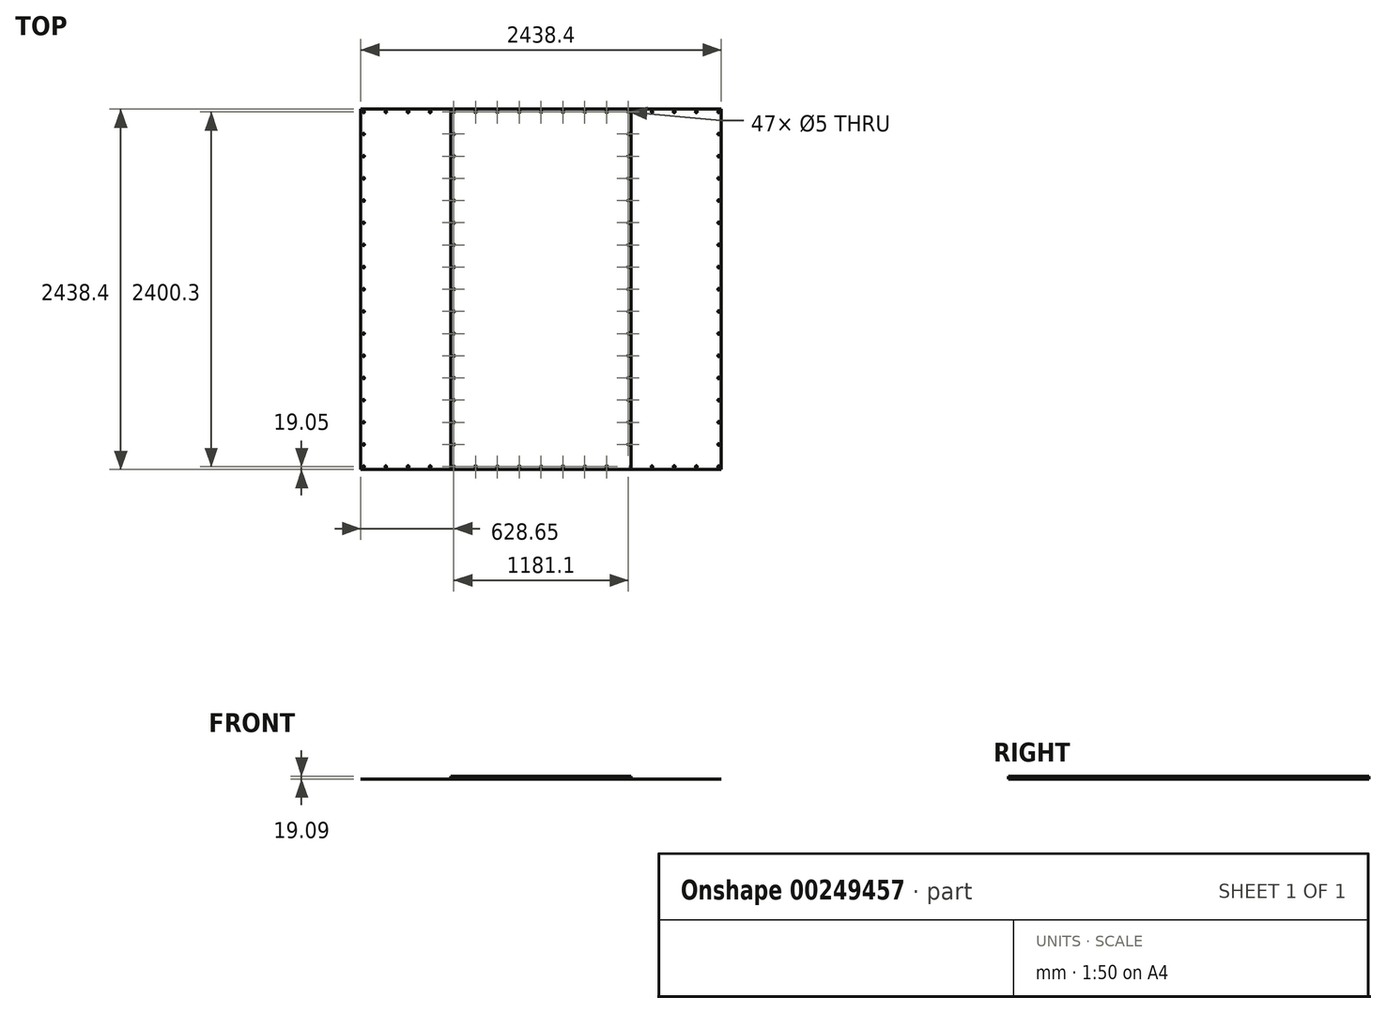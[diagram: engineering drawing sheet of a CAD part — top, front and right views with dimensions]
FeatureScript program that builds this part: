
annotation { "Feature Type Name" : "Feature", "Feature Type Description" : "" }
export const myFeature = defineFeature(function(context is Context, id is Id, definition is map)
    precondition{}
    {
        {
            var Q0;
            Q0=qCreatedBy(makeId("Top.planeOp"),FACE);
            var sketch = newSketch(context, id + "F0", { "sketchPlane" : qUnion([Q0])});
            skLineSegment(sketch, "E0.bottom", {"start": v(0, 1219.2) * mm, "end": v(1219.2, 1219.2) * mm});
            skLineSegment(sketch, "E0.top", {"start": v(0, -1219.2) * mm, "end": v(1219.2, -1219.2) * mm});
            skLineSegment(sketch, "E0.left", {"start": v(0, 1219.2) * mm, "end": v(0, -1219.2) * mm});
            skLineSegment(sketch, "E0.right", {"start": v(1219.2, 1219.2) * mm, "end": v(1219.2, -1219.2) * mm});
            skLineSegment(sketch, "E1", {"start": v(1219.2, 0) * mm, "end": v(0, 0) * mm});
            skSolve(sketch);
        }
        {
            var Q0;
            Q0 = qSketchRegion(id + "F0", true);
            extrude(context, id + "F1", {"entities" : qUnion([Q0]), "depth" : 5 / 203.2 * mm});
        }
        {
            var Q0;
            Q0=qCreatedBy(makeId("Top.planeOp"),FACE);
            var sketch = newSketch(context, id + "F2", { "sketchPlane" : qUnion([Q0])});
            skLineSegment(sketch, "E2.bottom", {"start": v(-1219.2, 1219.2) * mm, "end": v(0, 1219.2) * mm});
            skLineSegment(sketch, "E2.top", {"start": v(-1219.2, -1219.2) * mm, "end": v(0, -1219.2) * mm});
            skLineSegment(sketch, "E2.left", {"start": v(-1219.2, 1219.2) * mm, "end": v(-1219.2, -1219.2) * mm});
            skLineSegment(sketch, "E2.right", {"start": v(0, 1219.2) * mm, "end": v(0, -1219.2) * mm});
            skSolve(sketch);
        }
        {
            var Q0;
            Q0 = qSketchRegion(id + "F2", true);
            extrude(context, id + "F3", {"entities" : qUnion([Q0]), "operationType" : NewBodyOperationType.ADD, "depth" : 5 / 203.2 * mm});
        }
        {
            var Q0;
            Q0=makeQuery(id+"F3.boolean.opBoolean","MERGE",FACE,{"derivedFrom":[makeQuery(id+"F1.opExtrude","CAP_FACE",FACE,{"disambiguationData":[OSD([sQuery(id+"F0.wireOp",EDGE,"E0.bottom"),sQuery(id+"F0.wireOp",EDGE,"E0.top"),sQuery(id+"F0.wireOp",EDGE,"E0.left"),sQuery(id+"F0.wireOp",EDGE,"E0.right")])],"isStart":true}),makeQuery(id+"F3.opExtrude","CAP_FACE",FACE,{"disambiguationData":[OSD([sQuery(id+"F2.wireOp",EDGE,"E2.bottom"),sQuery(id+"F2.wireOp",EDGE,"E2.top"),sQuery(id+"F2.wireOp",EDGE,"E2.left"),sQuery(id+"F2.wireOp",EDGE,"E2.right")])],"isStart":true})]});
            var sketch = newSketch(context, id + "F4", { "sketchPlane" : qUnion([Q0])});
            skLineSegment(sketch, "E3.bottom", {"start": v(1219.2, -1219.2) * mm, "end": v(-1219.2, -1219.2) * mm});
            skLineSegment(sketch, "E3.top", {"start": v(1219.2, 0) * mm, "end": v(-1219.2, 0) * mm});
            skLineSegment(sketch, "E3.left", {"start": v(1219.2, -1219.2) * mm, "end": v(1219.2, 0) * mm});
            skLineSegment(sketch, "E3.right", {"start": v(-1219.2, -1219.2) * mm, "end": v(-1219.2, 0) * mm});
            skSolve(sketch);
        }
        {
            var Q0;
            Q0 = qSketchRegion(id + "F4", true);
            extrude(context, id + "F5", {"entities" : qUnion([Q0]), "operationType" : NewBodyOperationType.ADD, "depth" : 5 / 203.2 * mm});
        }
        {
            var Q0;
            Q0=makeQuery(id+"F3.boolean.opBoolean","MERGE",FACE,{"derivedFrom":[makeQuery(id+"F1.opExtrude","CAP_FACE",FACE,{"disambiguationData":[OSD([sQuery(id+"F0.wireOp",EDGE,"E0.bottom"),sQuery(id+"F0.wireOp",EDGE,"E0.top"),sQuery(id+"F0.wireOp",EDGE,"E0.left"),sQuery(id+"F0.wireOp",EDGE,"E0.right")])],"isStart":true}),makeQuery(id+"F3.opExtrude","CAP_FACE",FACE,{"disambiguationData":[OSD([sQuery(id+"F2.wireOp",EDGE,"E2.bottom"),sQuery(id+"F2.wireOp",EDGE,"E2.top"),sQuery(id+"F2.wireOp",EDGE,"E2.left"),sQuery(id+"F2.wireOp",EDGE,"E2.right")])],"isStart":true})]});
            var sketch = newSketch(context, id + "F6", { "sketchPlane" : qUnion([Q0])});
            skLineSegment(sketch, "E4.bottom", {"start": v(-1219.2, 1219.2) * mm, "end": v(1219.2, 1219.2) * mm});
            skLineSegment(sketch, "E4.top", {"start": v(-1219.2, 0) * mm, "end": v(1219.2, 0) * mm});
            skLineSegment(sketch, "E4.left", {"start": v(-1219.2, 1219.2) * mm, "end": v(-1219.2, 0) * mm});
            skLineSegment(sketch, "E4.right", {"start": v(1219.2, 1219.2) * mm, "end": v(1219.2, 0) * mm});
            skSolve(sketch);
        }
        {
            var Q0;
            Q0 = qSketchRegion(id + "F6", true);
            extrude(context, id + "F7", {"entities" : qUnion([Q0]), "operationType" : NewBodyOperationType.ADD, "depth" : 5 / 203.2 * mm});
        }
        {
            var Q0;
            Q0=makeQuery(id+"F3.boolean.opBoolean","MERGE",FACE,{"derivedFrom":[makeQuery(id+"F1.opExtrude","CAP_FACE",FACE,{"disambiguationData":[OSD([sQuery(id+"F0.wireOp",EDGE,"E0.bottom"),sQuery(id+"F0.wireOp",EDGE,"E0.top"),sQuery(id+"F0.wireOp",EDGE,"E0.left"),sQuery(id+"F0.wireOp",EDGE,"E0.right")])],"isStart":false}),makeQuery(id+"F3.opExtrude","CAP_FACE",FACE,{"disambiguationData":[OSD([sQuery(id+"F2.wireOp",EDGE,"E2.bottom"),sQuery(id+"F2.wireOp",EDGE,"E2.top"),sQuery(id+"F2.wireOp",EDGE,"E2.left"),sQuery(id+"F2.wireOp",EDGE,"E2.right")])],"isStart":false})]});
            var sketch = newSketch(context, id + "F8", { "sketchPlane" : qUnion([Q0])});
            skLineSegment(sketch, "E5", {"start": v(-1219.2, -1219.2) * mm, "end": v(-1200.15, -1200.15) * mm});
            skLineSegment(sketch, "E6", {"start": v(-1200.15, -1200.15) * mm, "end": v(-1050.13, -1200.15) * mm});
            skLineSegment(sketch, "E7", {"start": v(-1050.13, -1200.15) * mm, "end": v(-900.11, -1200.15) * mm});
            skLineSegment(sketch, "E8", {"start": v(-900.11, -1200.15) * mm, "end": v(-750.1, -1200.15) * mm});
            skLineSegment(sketch, "E9", {"start": v(-750.1, -1200.15) * mm, "end": v(-600.08, -1200.15) * mm});
            skLineSegment(sketch, "E10", {"start": v(-600.08, -1200.15) * mm, "end": v(-450.06, -1200.15) * mm});
            skLineSegment(sketch, "E11", {"start": v(-450.06, -1200.15) * mm, "end": v(-300.04, -1200.15) * mm});
            skLineSegment(sketch, "E12", {"start": v(-300.04, -1200.15) * mm, "end": v(-150.02, -1200.15) * mm});
            skLineSegment(sketch, "E13", {"start": v(-150.02, -1200.15) * mm, "end": v(0, -1200.15) * mm});
            skLineSegment(sketch, "E14", {"start": v(0, -1200.15) * mm, "end": v(150.02, -1200.15) * mm});
            skLineSegment(sketch, "E15", {"start": v(150.02, -1200.15) * mm, "end": v(300.04, -1200.15) * mm});
            skLineSegment(sketch, "E16", {"start": v(300.04, -1200.15) * mm, "end": v(450.06, -1200.15) * mm});
            skLineSegment(sketch, "E17", {"start": v(450.06, -1200.15) * mm, "end": v(600.07, -1200.15) * mm});
            skLineSegment(sketch, "E18", {"start": v(600.07, -1200.15) * mm, "end": v(750.1, -1200.15) * mm});
            skLineSegment(sketch, "E19", {"start": v(750.1, -1200.15) * mm, "end": v(900.11, -1200.15) * mm});
            skLineSegment(sketch, "E20", {"start": v(900.11, -1200.15) * mm, "end": v(1050.13, -1200.15) * mm});
            skLineSegment(sketch, "E21", {"start": v(1050.13, -1200.15) * mm, "end": v(1200.15, -1200.15) * mm});
            skLineSegment(sketch, "E22", {"start": v(1200.15, -1200.15) * mm, "end": v(1219.2, -1219.2) * mm});
            skLineSegment(sketch, "E23", {"start": v(-1200.15, 1200.15) * mm, "end": v(-1219.2, 1219.2) * mm});
            skLineSegment(sketch, "E24", {"start": v(-1200.15, 1200.15) * mm, "end": v(-1050.13, 1200.15) * mm});
            skLineSegment(sketch, "E25", {"start": v(-1050.13, 1200.15) * mm, "end": v(-900.11, 1200.15) * mm});
            skLineSegment(sketch, "E26", {"start": v(-900.11, 1200.15) * mm, "end": v(-750.1, 1200.15) * mm});
            skLineSegment(sketch, "E27", {"start": v(-750.1, 1200.15) * mm, "end": v(-600.08, 1200.15) * mm});
            skLineSegment(sketch, "E28", {"start": v(-600.08, 1200.15) * mm, "end": v(-450.06, 1200.15) * mm});
            skLineSegment(sketch, "E29", {"start": v(-450.06, 1200.15) * mm, "end": v(-300.04, 1200.15) * mm});
            skLineSegment(sketch, "E30", {"start": v(-300.04, 1200.15) * mm, "end": v(-150.02, 1200.15) * mm});
            skLineSegment(sketch, "E31", {"start": v(-150.02, 1200.15) * mm, "end": v(0, 1200.15) * mm});
            skLineSegment(sketch, "E32", {"start": v(0, 1200.15) * mm, "end": v(150.02, 1200.15) * mm});
            skLineSegment(sketch, "E33", {"start": v(150.02, 1200.15) * mm, "end": v(300.04, 1200.15) * mm});
            skLineSegment(sketch, "E34", {"start": v(300.04, 1200.15) * mm, "end": v(450.06, 1200.15) * mm});
            skLineSegment(sketch, "E35", {"start": v(450.06, 1200.15) * mm, "end": v(600.08, 1200.15) * mm});
            skLineSegment(sketch, "E36", {"start": v(600.08, 1200.15) * mm, "end": v(750.1, 1200.15) * mm});
            skLineSegment(sketch, "E37", {"start": v(750.1, 1200.15) * mm, "end": v(900.11, 1200.15) * mm});
            skLineSegment(sketch, "E38", {"start": v(900.11, 1200.15) * mm, "end": v(1050.13, 1200.15) * mm});
            skLineSegment(sketch, "E39", {"start": v(1050.13, 1200.15) * mm, "end": v(1200.15, 1200.15) * mm});
            skLineSegment(sketch, "E40", {"start": v(1200.15, 1200.15) * mm, "end": v(1219.2, 1219.2) * mm});
            skLineSegment(sketch, "E41", {"start": v(1219.2, -1219.2) * mm, "end": v(1200.15, -1200.15) * mm});
            skLineSegment(sketch, "E42", {"start": v(1200.15, -1200.15) * mm, "end": v(1200.15, -1050.13) * mm});
            skLineSegment(sketch, "E43", {"start": v(1200.15, -1050.13) * mm, "end": v(1200.15, -900.11) * mm});
            skLineSegment(sketch, "E44", {"start": v(1200.15, -900.11) * mm, "end": v(1200.15, -750.1) * mm});
            skLineSegment(sketch, "E45", {"start": v(1200.15, -750.1) * mm, "end": v(1200.15, -600.07) * mm});
            skLineSegment(sketch, "E46", {"start": v(1200.15, -600.07) * mm, "end": v(1200.15, -450.06) * mm});
            skLineSegment(sketch, "E47", {"start": v(1200.15, -450.06) * mm, "end": v(1200.15, -300.04) * mm});
            skLineSegment(sketch, "E48", {"start": v(1200.15, -300.04) * mm, "end": v(1200.15, -150.02) * mm});
            skLineSegment(sketch, "E49", {"start": v(1200.15, -150.02) * mm, "end": v(1200.15, 0) * mm});
            skLineSegment(sketch, "E50", {"start": v(1200.15, 0) * mm, "end": v(1200.15, 150.02) * mm});
            skLineSegment(sketch, "E51", {"start": v(1200.15, 150.02) * mm, "end": v(1200.15, 300.04) * mm});
            skLineSegment(sketch, "E52", {"start": v(1200.15, 300.04) * mm, "end": v(1200.15, 450.06) * mm});
            skLineSegment(sketch, "E53", {"start": v(1200.15, 450.06) * mm, "end": v(1200.15, 600.08) * mm});
            skLineSegment(sketch, "E54", {"start": v(1200.15, 600.08) * mm, "end": v(1200.15, 750.1) * mm});
            skLineSegment(sketch, "E55", {"start": v(1200.15, 750.1) * mm, "end": v(1200.15, 900.11) * mm});
            skLineSegment(sketch, "E56", {"start": v(1200.15, 900.11) * mm, "end": v(1200.15, 1050.13) * mm});
            skLineSegment(sketch, "E57", {"start": v(1200.15, 1050.13) * mm, "end": v(1200.15, 1200.15) * mm});
            skLineSegment(sketch, "E58", {"start": v(-1219.2, 1219.2) * mm, "end": v(-1200.15, 1200.15) * mm});
            skLineSegment(sketch, "E59", {"start": v(-1200.15, 1200.15) * mm, "end": v(-1200.15, 1050.13) * mm});
            skLineSegment(sketch, "E60", {"start": v(-1200.15, 1050.13) * mm, "end": v(-1200.15, 900.11) * mm});
            skLineSegment(sketch, "E61", {"start": v(-1200.15, 900.11) * mm, "end": v(-1200.15, 750.1) * mm});
            skLineSegment(sketch, "E62", {"start": v(-1200.15, 750.1) * mm, "end": v(-1200.15, 600.07) * mm});
            skLineSegment(sketch, "E63", {"start": v(-1200.15, 600.07) * mm, "end": v(-1200.15, 450.06) * mm});
            skLineSegment(sketch, "E64", {"start": v(-1200.15, 450.06) * mm, "end": v(-1200.15, 300.04) * mm});
            skLineSegment(sketch, "E65", {"start": v(-1200.15, 300.04) * mm, "end": v(-1200.15, 150.02) * mm});
            skLineSegment(sketch, "E66", {"start": v(-1200.15, 150.02) * mm, "end": v(-1200.15, 0) * mm});
            skLineSegment(sketch, "E67", {"start": v(-1200.15, 0) * mm, "end": v(-1200.15, -150.02) * mm});
            skLineSegment(sketch, "E68", {"start": v(-1200.15, -150.02) * mm, "end": v(-1200.15, -300.04) * mm});
            skLineSegment(sketch, "E69", {"start": v(-1200.15, -300.04) * mm, "end": v(-1200.15, -450.06) * mm});
            skLineSegment(sketch, "E70", {"start": v(-1200.15, -450.06) * mm, "end": v(-1200.15, -600.08) * mm});
            skLineSegment(sketch, "E71", {"start": v(-1200.15, -600.08) * mm, "end": v(-1200.15, -750.1) * mm});
            skLineSegment(sketch, "E72", {"start": v(-1200.15, -750.1) * mm, "end": v(-1200.15, -900.11) * mm});
            skLineSegment(sketch, "E73", {"start": v(-1200.15, -900.11) * mm, "end": v(-1200.15, -1050.13) * mm});
            skLineSegment(sketch, "E74", {"start": v(-1200.15, -1050.13) * mm, "end": v(-1200.15, -1200.15) * mm});
            skLineSegment(sketch, "E75", {"start": v(-1200.15, -1200.15) * mm, "end": v(-1219.2, -1219.2) * mm});
            skSolve(sketch);
        }
        {
            var Q0;
            Q0=sQuery(id+"F8.wireOp",VERTEX,"E63.start");
            var Q1;
            Q1=sQuery(id+"F8.wireOp",VERTEX,"E64.start");
            var Q2;
            Q2=sQuery(id+"F8.wireOp",VERTEX,"E65.start");
            var Q3;
            Q3=sQuery(id+"F8.wireOp",VERTEX,"E66.start");
            var Q4;
            Q4=sQuery(id+"F8.wireOp",VERTEX,"E67.start");
            var Q5;
            Q5=sQuery(id+"F8.wireOp",VERTEX,"E68.start");
            var Q6;
            Q6=sQuery(id+"F8.wireOp",VERTEX,"E68.end");
            var Q7;
            Q7=sQuery(id+"F8.wireOp",VERTEX,"E70.start");
            var Q8;
            Q8=sQuery(id+"F8.wireOp",VERTEX,"E71.start");
            var Q9;
            Q9=sQuery(id+"F8.wireOp",VERTEX,"E72.start");
            var Q10;
            Q10=sQuery(id+"F8.wireOp",VERTEX,"E73.start");
            var Q11;
            Q11=sQuery(id+"F8.wireOp",VERTEX,"E74.start");
            var Q12;
            Q12=sQuery(id+"F8.wireOp",VERTEX,"E75.start");
            var Q13;
            Q13=sQuery(id+"F8.wireOp",VERTEX,"E7.start");
            var Q14;
            Q14=sQuery(id+"F8.wireOp",VERTEX,"E8.start");
            var Q15;
            Q15=sQuery(id+"F8.wireOp",VERTEX,"E9.start");
            var Q16;
            Q16=sQuery(id+"F8.wireOp",VERTEX,"E10.start");
            var Q17;
            Q17=sQuery(id+"F8.wireOp",VERTEX,"E11.start");
            var Q18;
            Q18=sQuery(id+"F8.wireOp",VERTEX,"E12.start");
            var Q19;
            Q19=sQuery(id+"F8.wireOp",VERTEX,"E13.start");
            var Q20;
            Q20=sQuery(id+"F8.wireOp",VERTEX,"E62.start");
            var Q21;
            Q21=sQuery(id+"F8.wireOp",VERTEX,"E60.end");
            var Q22;
            Q22=sQuery(id+"F8.wireOp",VERTEX,"E60.start");
            var Q23;
            Q23=sQuery(id+"F8.wireOp",VERTEX,"E24.start");
            var Q24;
            Q24=sQuery(id+"F8.wireOp",VERTEX,"E25.start");
            var Q25;
            Q25=sQuery(id+"F8.wireOp",VERTEX,"E26.start");
            var Q26;
            Q26=sQuery(id+"F8.wireOp",VERTEX,"E27.start");
            var Q27;
            Q27=sQuery(id+"F8.wireOp",VERTEX,"E28.start");
            var Q28;
            Q28=sQuery(id+"F8.wireOp",VERTEX,"E29.start");
            var Q29;
            Q29=sQuery(id+"F8.wireOp",VERTEX,"E29.end");
            var Q30;
            Q30=sQuery(id+"F8.wireOp",VERTEX,"E31.start");
            var Q31;
            Q31=sQuery(id+"F8.wireOp",VERTEX,"E32.start");
            var Q32;
            Q32=sQuery(id+"F8.wireOp",VERTEX,"E33.start");
            var Q33;
            Q33=sQuery(id+"F8.wireOp",VERTEX,"E34.start");
            var Q34;
            Q34=sQuery(id+"F8.wireOp",VERTEX,"E35.start");
            var Q35;
            Q35=sQuery(id+"F8.wireOp",VERTEX,"E36.start");
            var Q36;
            Q36=sQuery(id+"F8.wireOp",VERTEX,"E37.start");
            var Q37;
            Q37=sQuery(id+"F8.wireOp",VERTEX,"E37.end");
            var Q38;
            Q38=sQuery(id+"F8.wireOp",VERTEX,"E39.start");
            var Q39;
            Q39=sQuery(id+"F8.wireOp",VERTEX,"E40.start");
            var Q40;
            Q40=sQuery(id+"F8.wireOp",VERTEX,"E57.start");
            var Q41;
            Q41=sQuery(id+"F8.wireOp",VERTEX,"E56.start");
            var Q42;
            Q42=sQuery(id+"F8.wireOp",VERTEX,"E55.start");
            var Q43;
            Q43=sQuery(id+"F8.wireOp",VERTEX,"E53.end");
            var Q44;
            Q44=sQuery(id+"F8.wireOp",VERTEX,"E53.start");
            var Q45;
            Q45=sQuery(id+"F8.wireOp",VERTEX,"E52.start");
            var Q46;
            Q46=sQuery(id+"F8.wireOp",VERTEX,"E51.start");
            var Q47;
            Q47=sQuery(id+"F8.wireOp",VERTEX,"E50.start");
            var Q48;
            Q48=sQuery(id+"F8.wireOp",VERTEX,"E49.start");
            var Q49;
            Q49=sQuery(id+"F8.wireOp",VERTEX,"E48.start");
            var Q50;
            Q50=sQuery(id+"F8.wireOp",VERTEX,"E47.start");
            var Q51;
            Q51=sQuery(id+"F8.wireOp",VERTEX,"E45.end");
            var Q52;
            Q52=sQuery(id+"F8.wireOp",VERTEX,"E45.start");
            var Q53;
            Q53=sQuery(id+"F8.wireOp",VERTEX,"E44.start");
            var Q54;
            Q54=sQuery(id+"F8.wireOp",VERTEX,"E43.start");
            var Q55;
            Q55=sQuery(id+"F8.wireOp",VERTEX,"E21.end");
            var Q56;
            Q56=sQuery(id+"F8.wireOp",VERTEX,"E21.start");
            var Q57;
            Q57=sQuery(id+"F8.wireOp",VERTEX,"E20.start");
            var Q58;
            Q58=sQuery(id+"F8.wireOp",VERTEX,"E19.start");
            var Q59;
            Q59=sQuery(id+"F8.wireOp",VERTEX,"E18.start");
            var Q60;
            Q60=sQuery(id+"F8.wireOp",VERTEX,"E17.start");
            var Q61;
            Q61=sQuery(id+"F8.wireOp",VERTEX,"E16.start");
            var Q62;
            Q62=sQuery(id+"F8.wireOp",VERTEX,"E15.start");
            var Q63;
            Q63=sQuery(id+"F8.wireOp",VERTEX,"E13.end");
            var Q64;
            Q64=sQuery(id+"F8.wireOp",VERTEX,"E13.end");
            var Q65;
            Q65=sQuery(id+"F8.wireOp",VERTEX,"E15.start");
            var Q66;
            Q66=sQuery(id+"F8.wireOp",VERTEX,"E16.start");
            var Q67;
            Q67=sQuery(id+"F8.wireOp",VERTEX,"E17.start");
            var Q68;
            Q68=sQuery(id+"F8.wireOp",VERTEX,"E18.start");
            var Q69;
            Q69=sQuery(id+"F8.wireOp",VERTEX,"E19.start");
            var Q70;
            Q70=sQuery(id+"F8.wireOp",VERTEX,"E20.start");
            var Q71;
            Q71=makeQuery(id+"F1.opExtrude","SWEPT_BODY",BODY,{"disambiguationData":[OSD([sQuery(id+"F0.wireOp",EDGE,"E0.bottom"),sQuery(id+"F0.wireOp",EDGE,"E0.top"),sQuery(id+"F0.wireOp",EDGE,"E0.left"),sQuery(id+"F0.wireOp",EDGE,"E0.right")])]});
            hole(context, id + "F9", {"style" : HoleStyle.C_SINK, "endStyle" : HoleEndStyle.THROUGH, "standardTappedOrClearance" : lookupTablePath({ "standard" : "ISO", "size" : "5", "type" : "Drilled" }), "standardBlindInLast" : lookupTablePath({ "standard" : "ISO", "size" : "5", "type" : "Drilled" }), "holeDiameter" : 5 * mm, "cSinkDiameter" : 11.2 * mm, "cSinkAngle" : 90 * degree, "tappedDepth" : 12.7 * mm, "tapClearance" : 3, "startFromSketch" : true, "locations" : qUnion([Q0, Q1, Q2, Q3, Q4, Q5, Q6, Q7, Q8, Q9, Q10, Q11, Q12, Q13, Q14, Q15, Q16, Q17, Q18, Q19, Q20, Q21, Q22, Q23, Q24, Q25, Q26, Q27, Q28, Q29, Q30, Q31, Q32, Q33, Q34, Q35, Q36, Q37, Q38, Q39, Q40, Q41, Q42, Q43, Q44, Q45, Q46, Q47, Q48, Q49, Q50, Q51, Q52, Q53, Q54, Q55, Q56, Q57, Q58, Q59, Q60, Q61, Q62, Q63, Q64, Q65, Q66, Q67, Q68, Q69, Q70]), "scope" : qUnion([Q71])});
        }
        {
            var Q0;
            Q0=makeQuery(id+"F3.boolean.opBoolean","MERGE",FACE,{"derivedFrom":[makeQuery(id+"F1.opExtrude","CAP_FACE",FACE,{"disambiguationData":[OSD([sQuery(id+"F0.wireOp",EDGE,"E0.bottom"),sQuery(id+"F0.wireOp",EDGE,"E0.top"),sQuery(id+"F0.wireOp",EDGE,"E0.left"),sQuery(id+"F0.wireOp",EDGE,"E0.right")])],"isStart":false}),makeQuery(id+"F3.opExtrude","CAP_FACE",FACE,{"disambiguationData":[OSD([sQuery(id+"F2.wireOp",EDGE,"E2.bottom"),sQuery(id+"F2.wireOp",EDGE,"E2.top"),sQuery(id+"F2.wireOp",EDGE,"E2.left"),sQuery(id+"F2.wireOp",EDGE,"E2.right")])],"isStart":false})]});
            var sketch = newSketch(context, id + "F10", { "sketchPlane" : qUnion([Q0])});
            skLineSegment(sketch, "E76.bottom", {"start": v(-609.6, 1219.2) * mm, "end": v(609.6, 1219.2) * mm});
            skLineSegment(sketch, "E76.top", {"start": v(-609.6, -1219.2) * mm, "end": v(609.6, -1219.2) * mm});
            skLineSegment(sketch, "E76.left", {"start": v(-609.6, 1219.2) * mm, "end": v(-609.6, -1219.2) * mm});
            skLineSegment(sketch, "E76.right", {"start": v(609.6, 1219.2) * mm, "end": v(609.6, -1219.2) * mm});
            skLineSegment(sketch, "E77", {"start": v(0, 0) * mm, "end": v(0, 1219.2) * mm});
            skSolve(sketch);
        }
        {
            var Q0;
            Q0 = qSketchRegion(id + "F10", true);
            extrude(context, id + "F11", {"entities" : qUnion([Q0]), "operationType" : NewBodyOperationType.ADD, "depth" : 19.05 * mm});
        }
        {
            var Q0;
            Q0=makeQuery(id+"F11.opExtrude","CAP_FACE",FACE,{"disambiguationData":[OSD([sQuery(id+"F10.wireOp",EDGE,"E76.bottom"),sQuery(id+"F10.wireOp",EDGE,"E76.top"),sQuery(id+"F10.wireOp",EDGE,"E76.left"),sQuery(id+"F10.wireOp",EDGE,"E76.right")])],"isStart":false});
            var sketch = newSketch(context, id + "F12", { "sketchPlane" : qUnion([Q0])});
            skLineSegment(sketch, "E78", {"start": v(-609.6, -1219.2) * mm, "end": v(-590.55, -1200.15) * mm});
            skLineSegment(sketch, "E79", {"start": v(-590.55, -1200.15) * mm, "end": v(-442.91, -1200.15) * mm});
            skLineSegment(sketch, "E80", {"start": v(-442.91, -1200.15) * mm, "end": v(-295.27, -1200.15) * mm});
            skLineSegment(sketch, "E81", {"start": v(-295.27, -1200.15) * mm, "end": v(-147.64, -1200.15) * mm});
            skLineSegment(sketch, "E82", {"start": v(-147.64, -1200.15) * mm, "end": v(0, -1200.15) * mm});
            skLineSegment(sketch, "E83", {"start": v(0, -1200.15) * mm, "end": v(147.64, -1200.15) * mm});
            skLineSegment(sketch, "E84", {"start": v(147.64, -1200.15) * mm, "end": v(295.28, -1200.15) * mm});
            skLineSegment(sketch, "E85", {"start": v(295.28, -1200.15) * mm, "end": v(442.91, -1200.15) * mm});
            skLineSegment(sketch, "E86", {"start": v(442.91, -1200.15) * mm, "end": v(590.55, -1200.15) * mm});
            skLineSegment(sketch, "E87", {"start": v(590.55, -1200.15) * mm, "end": v(609.6, -1219.2) * mm});
            skLineSegment(sketch, "E88", {"start": v(609.6, 1219.2) * mm, "end": v(590.55, 1200.15) * mm});
            skLineSegment(sketch, "E89", {"start": v(590.55, 1200.15) * mm, "end": v(442.91, 1200.15) * mm});
            skLineSegment(sketch, "E90", {"start": v(442.91, 1200.15) * mm, "end": v(295.27, 1200.15) * mm});
            skLineSegment(sketch, "E91", {"start": v(295.27, 1200.15) * mm, "end": v(147.64, 1200.15) * mm});
            skLineSegment(sketch, "E92", {"start": v(147.64, 1200.15) * mm, "end": v(0, 1200.15) * mm});
            skLineSegment(sketch, "E93", {"start": v(0, 1200.15) * mm, "end": v(-147.64, 1200.15) * mm});
            skLineSegment(sketch, "E94", {"start": v(-147.64, 1200.15) * mm, "end": v(-295.28, 1200.15) * mm});
            skLineSegment(sketch, "E95", {"start": v(-295.28, 1200.15) * mm, "end": v(-442.91, 1200.15) * mm});
            skLineSegment(sketch, "E96", {"start": v(-442.91, 1200.15) * mm, "end": v(-590.55, 1200.15) * mm});
            skLineSegment(sketch, "E97", {"start": v(-590.55, 1200.15) * mm, "end": v(-609.6, 1219.2) * mm});
            skLineSegment(sketch, "E98", {"start": v(-590.55, 1200.15) * mm, "end": v(-590.55, 1050.13) * mm});
            skLineSegment(sketch, "E99", {"start": v(-590.55, 1050.13) * mm, "end": v(-590.55, 900.11) * mm});
            skLineSegment(sketch, "E100", {"start": v(-590.55, 900.11) * mm, "end": v(-590.55, 750.1) * mm});
            skLineSegment(sketch, "E101", {"start": v(-590.55, 750.1) * mm, "end": v(-590.55, 600.08) * mm});
            skLineSegment(sketch, "E102", {"start": v(-590.55, 600.08) * mm, "end": v(-590.55, 450.06) * mm});
            skLineSegment(sketch, "E103", {"start": v(-590.55, 450.06) * mm, "end": v(-590.55, 300.04) * mm});
            skLineSegment(sketch, "E104", {"start": v(-590.55, 300.04) * mm, "end": v(-590.55, 150.02) * mm});
            skLineSegment(sketch, "E105", {"start": v(-590.55, 150.02) * mm, "end": v(-590.55, 0) * mm});
            skLineSegment(sketch, "E106", {"start": v(-590.55, 0) * mm, "end": v(-590.55, -150.02) * mm});
            skLineSegment(sketch, "E107", {"start": v(-590.55, -150.02) * mm, "end": v(-590.55, -300.04) * mm});
            skLineSegment(sketch, "E108", {"start": v(-590.55, -300.04) * mm, "end": v(-590.55, -450.06) * mm});
            skLineSegment(sketch, "E109", {"start": v(-590.55, -450.06) * mm, "end": v(-590.55, -600.07) * mm});
            skLineSegment(sketch, "E110", {"start": v(-590.55, -600.07) * mm, "end": v(-590.55, -750.1) * mm});
            skLineSegment(sketch, "E111", {"start": v(-590.55, -750.1) * mm, "end": v(-590.55, -900.11) * mm});
            skLineSegment(sketch, "E112", {"start": v(-590.55, -900.11) * mm, "end": v(-590.55, -1050.13) * mm});
            skLineSegment(sketch, "E113", {"start": v(-590.55, -1050.13) * mm, "end": v(-590.55, -1200.15) * mm});
            skLineSegment(sketch, "E114", {"start": v(590.55, -1200.15) * mm, "end": v(590.55, -1050.13) * mm});
            skLineSegment(sketch, "E115", {"start": v(590.55, -1050.13) * mm, "end": v(590.55, -900.11) * mm});
            skLineSegment(sketch, "E116", {"start": v(590.55, -900.11) * mm, "end": v(590.55, -750.1) * mm});
            skLineSegment(sketch, "E117", {"start": v(590.55, -750.1) * mm, "end": v(590.55, -600.08) * mm});
            skLineSegment(sketch, "E118", {"start": v(590.55, -600.08) * mm, "end": v(590.55, -450.06) * mm});
            skLineSegment(sketch, "E119", {"start": v(590.55, -450.06) * mm, "end": v(590.55, -300.04) * mm});
            skLineSegment(sketch, "E120", {"start": v(590.55, -300.04) * mm, "end": v(590.55, -150.02) * mm});
            skLineSegment(sketch, "E121", {"start": v(590.55, -150.02) * mm, "end": v(590.55, 0) * mm});
            skLineSegment(sketch, "E122", {"start": v(590.55, 0) * mm, "end": v(590.55, 150.02) * mm});
            skLineSegment(sketch, "E123", {"start": v(590.55, 150.02) * mm, "end": v(590.55, 300.04) * mm});
            skLineSegment(sketch, "E124", {"start": v(590.55, 300.04) * mm, "end": v(590.55, 450.06) * mm});
            skLineSegment(sketch, "E125", {"start": v(590.55, 450.06) * mm, "end": v(590.55, 600.07) * mm});
            skLineSegment(sketch, "E126", {"start": v(590.55, 600.07) * mm, "end": v(590.55, 750.1) * mm});
            skLineSegment(sketch, "E127", {"start": v(590.55, 750.1) * mm, "end": v(590.55, 900.11) * mm});
            skLineSegment(sketch, "E128", {"start": v(590.55, 900.11) * mm, "end": v(590.55, 1050.13) * mm});
            skLineSegment(sketch, "E129", {"start": v(590.55, 1050.13) * mm, "end": v(590.55, 1200.15) * mm});
            skSolve(sketch);
        }
        {
            var Q0;
            Q0=sQuery(id+"F12.wireOp",VERTEX,"E98.start");
            var Q1;
            Q1=sQuery(id+"F12.wireOp",VERTEX,"E95.end");
            var Q2;
            Q2=sQuery(id+"F12.wireOp",VERTEX,"E94.end");
            var Q3;
            Q3=sQuery(id+"F12.wireOp",VERTEX,"E94.start");
            var Q4;
            Q4=sQuery(id+"F12.wireOp",VERTEX,"E92.end");
            var Q5;
            Q5=sQuery(id+"F12.wireOp",VERTEX,"E91.end");
            var Q6;
            Q6=sQuery(id+"F12.wireOp",VERTEX,"E91.start");
            var Q7;
            Q7=sQuery(id+"F12.wireOp",VERTEX,"E89.end");
            var Q8;
            Q8=sQuery(id+"F12.wireOp",VERTEX,"E129.start");
            var Q9;
            Q9=sQuery(id+"F12.wireOp",VERTEX,"E129.end");
            var Q10;
            Q10=sQuery(id+"F12.wireOp",VERTEX,"E127.end");
            var Q11;
            Q11=sQuery(id+"F12.wireOp",VERTEX,"E126.end");
            var Q12;
            Q12=sQuery(id+"F12.wireOp",VERTEX,"E125.end");
            var Q13;
            Q13=sQuery(id+"F12.wireOp",VERTEX,"E124.end");
            var Q14;
            Q14=sQuery(id+"F12.wireOp",VERTEX,"E124.start");
            var Q15;
            Q15=sQuery(id+"F12.wireOp",VERTEX,"E122.end");
            var Q16;
            Q16=sQuery(id+"F12.wireOp",VERTEX,"E121.end");
            var Q17;
            Q17=sQuery(id+"F12.wireOp",VERTEX,"E121.start");
            var Q18;
            Q18=sQuery(id+"F12.wireOp",VERTEX,"E119.end");
            var Q19;
            Q19=sQuery(id+"F12.wireOp",VERTEX,"E118.end");
            var Q20;
            Q20=sQuery(id+"F12.wireOp",VERTEX,"E117.end");
            var Q21;
            Q21=sQuery(id+"F12.wireOp",VERTEX,"E116.end");
            var Q22;
            Q22=sQuery(id+"F12.wireOp",VERTEX,"E116.start");
            var Q23;
            Q23=sQuery(id+"F12.wireOp",VERTEX,"E114.end");
            var Q24;
            Q24=sQuery(id+"F12.wireOp",VERTEX,"E87.start");
            var Q25;
            Q25=sQuery(id+"F12.wireOp",VERTEX,"E85.end");
            var Q26;
            Q26=sQuery(id+"F12.wireOp",VERTEX,"E84.end");
            var Q27;
            Q27=sQuery(id+"F12.wireOp",VERTEX,"E84.start");
            var Q28;
            Q28=sQuery(id+"F12.wireOp",VERTEX,"E83.start");
            var Q29;
            Q29=sQuery(id+"F12.wireOp",VERTEX,"E82.start");
            var Q30;
            Q30=sQuery(id+"F12.wireOp",VERTEX,"E80.end");
            var Q31;
            Q31=sQuery(id+"F12.wireOp",VERTEX,"E80.start");
            var Q32;
            Q32=sQuery(id+"F12.wireOp",VERTEX,"E79.start");
            var Q33;
            Q33=sQuery(id+"F12.wireOp",VERTEX,"E112.end");
            var Q34;
            Q34=sQuery(id+"F12.wireOp",VERTEX,"E111.end");
            var Q35;
            Q35=sQuery(id+"F12.wireOp",VERTEX,"E110.end");
            var Q36;
            Q36=sQuery(id+"F12.wireOp",VERTEX,"E110.start");
            var Q37;
            Q37=sQuery(id+"F12.wireOp",VERTEX,"E108.end");
            var Q38;
            Q38=sQuery(id+"F12.wireOp",VERTEX,"E107.end");
            var Q39;
            Q39=sQuery(id+"F12.wireOp",VERTEX,"E107.start");
            var Q40;
            Q40=sQuery(id+"F12.wireOp",VERTEX,"E105.end");
            var Q41;
            Q41=sQuery(id+"F12.wireOp",VERTEX,"E104.end");
            var Q42;
            Q42=sQuery(id+"F12.wireOp",VERTEX,"E103.end");
            var Q43;
            Q43=sQuery(id+"F12.wireOp",VERTEX,"E102.end");
            var Q44;
            Q44=sQuery(id+"F12.wireOp",VERTEX,"E102.start");
            var Q45;
            Q45=sQuery(id+"F12.wireOp",VERTEX,"E100.end");
            var Q46;
            Q46=sQuery(id+"F12.wireOp",VERTEX,"E99.end");
            var Q47;
            Q47=sQuery(id+"F12.wireOp",VERTEX,"E99.start");
            var Q48;
            Q48=sQuery(id+"F12.wireOp",VERTEX,"E110.end");
            var Q49;
            Q49=sQuery(id+"F12.wireOp",VERTEX,"E110.start");
            var Q50;
            Q50=sQuery(id+"F12.wireOp",VERTEX,"E108.end");
            var Q51;
            Q51=sQuery(id+"F12.wireOp",VERTEX,"E107.end");
            var Q52;
            Q52=sQuery(id+"F12.wireOp",VERTEX,"E107.start");
            var Q53;
            Q53=sQuery(id+"F12.wireOp",VERTEX,"E105.end");
            var Q54;
            Q54=sQuery(id+"F12.wireOp",VERTEX,"E104.end");
            var Q55;
            Q55=sQuery(id+"F12.wireOp",VERTEX,"E103.end");
            var Q56;
            Q56=sQuery(id+"F12.wireOp",VERTEX,"E102.end");
            var Q57;
            Q57=sQuery(id+"F12.wireOp",VERTEX,"E102.start");
            var Q58;
            Q58=sQuery(id+"F12.wireOp",VERTEX,"E100.end");
            var Q59;
            Q59=sQuery(id+"F12.wireOp",VERTEX,"E99.end");
            var Q60;
            Q60=sQuery(id+"F12.wireOp",VERTEX,"E99.start");
            var Q61;
            Q61=makeQuery(id+"F1.opExtrude","SWEPT_BODY",BODY,{"disambiguationData":[OSD([sQuery(id+"F0.wireOp",EDGE,"E0.bottom"),sQuery(id+"F0.wireOp",EDGE,"E0.top"),sQuery(id+"F0.wireOp",EDGE,"E0.left"),sQuery(id+"F0.wireOp",EDGE,"E0.right")])]});
            hole(context, id + "F13", {"style" : HoleStyle.C_SINK, "endStyle" : HoleEndStyle.THROUGH, "standardTappedOrClearance" : lookupTablePath({ "standard" : "ISO", "size" : "5", "type" : "Drilled" }), "standardBlindInLast" : lookupTablePath({ "standard" : "ISO", "size" : "5", "type" : "Drilled" }), "holeDiameter" : 5 * mm, "cSinkDiameter" : 11.2 * mm, "cSinkAngle" : 90 * degree, "tappedDepth" : 12.7 * mm, "tapClearance" : 3, "startFromSketch" : true, "locations" : qUnion([Q0, Q1, Q2, Q3, Q4, Q5, Q6, Q7, Q8, Q9, Q10, Q11, Q12, Q13, Q14, Q15, Q16, Q17, Q18, Q19, Q20, Q21, Q22, Q23, Q24, Q25, Q26, Q27, Q28, Q29, Q30, Q31, Q32, Q33, Q34, Q35, Q36, Q37, Q38, Q39, Q40, Q41, Q42, Q43, Q44, Q45, Q46, Q47, Q48, Q49, Q50, Q51, Q52, Q53, Q54, Q55, Q56, Q57, Q58, Q59, Q60]), "scope" : qUnion([Q61])});
        }
    });
